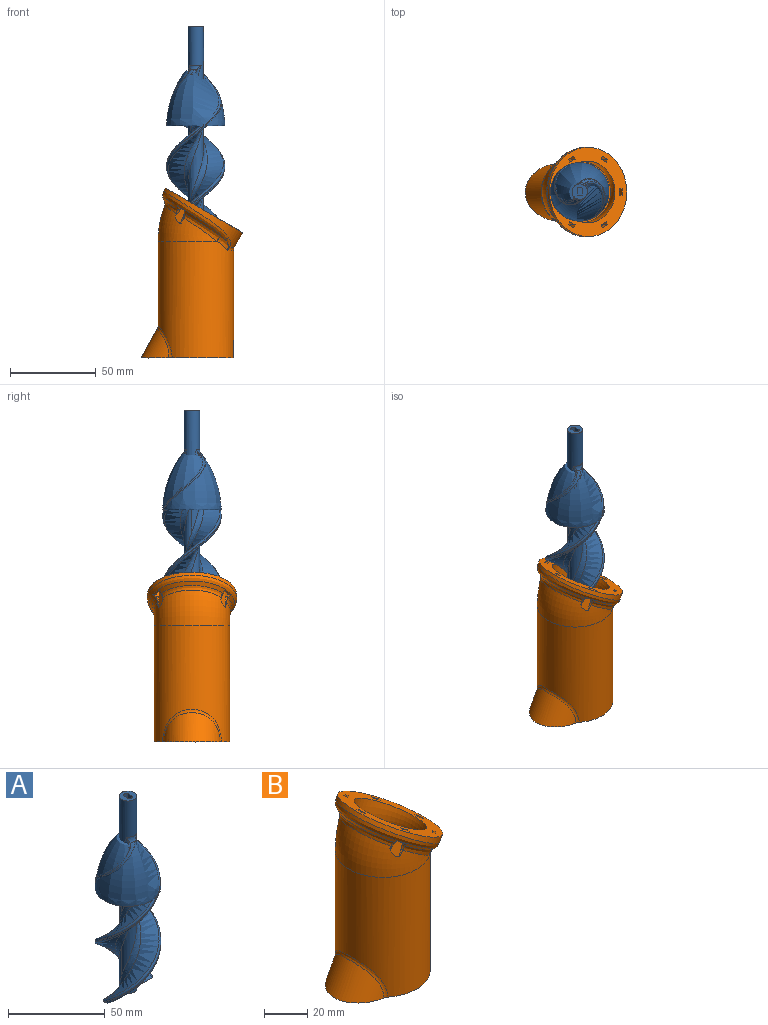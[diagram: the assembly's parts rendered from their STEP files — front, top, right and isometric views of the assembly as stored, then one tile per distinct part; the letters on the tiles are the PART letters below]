
ASSEMBLY  parts=2 mates=1
PART A: 42 faces, bbox 35.1x35.4x126.7 mm
  f0: bspline ~97.14x34.68mm, area 986.1mm2, adj f3,f23,f32,f33
  f1: bspline ~97.14x34.68mm, area 986.1mm2, adj f3,f18,f36,f37
  f2: revolved ~33.25x32.4mm, area 47.3mm2, adj f5,f19,f29,f30,f37,f38
  f3: plane 34.42x9.42mm, normal (0,0,-1), area 165.5mm2, adj f0,f1,f4,f5,f6,f7,f9,f11
  f4: bspline ~97.14x34.68mm, area 1003.5mm2, adj f3,f20,f28,f29
  f5: bspline ~68.57x34.96mm, area 53.1mm2, adj f2,f3,f28,f36
  f6: bspline ~97.14x34.68mm, area 1003.4mm2, adj f3,f21,f24,f25
  f7: bspline ~68.57x34.96mm, area 53.1mm2, adj f3,f8,f24,f32
  f8: revolved ~33.25x32.4mm, area 47.3mm2, adj f7,f22,f25,f26,f33,f34
  f9: cylinder r=4.5mm len=29.09mm, axis (0,0,-1), area 128.4mm2, adj f3,f10,f20,f23
  f10: cylinder r=4.5mm len=111.09mm, axis (0,0,-1), area 1408.2mm2, adj f9,f11,f12,f18,f19,f20,f21,f22
  f11: cylinder r=4.5mm len=69.09mm, axis (0,0,-1), area 385.1mm2, adj f3,f10,f18,f21
  f12: plane 9x9mm, normal (0,0,1), area 49.6mm2, adj f10,f13,f14,f15,f16
  f13: plane 6x4mm, normal (-1,0,0), area 24mm2, adj f12,f14,f16,f17
  f14: cylinder r=2.5mm len=6mm, axis (0,0,1), area 19.3mm2, adj f12,f13,f15,f17
  f15: plane 6x4mm, normal (1,0,0), area 24mm2, adj f12,f14,f16,f17
  f16: cylinder r=2.5mm len=6mm, axis (0,0,1), area 19.3mm2, adj f12,f13,f15,f17
  f17: plane 5x3mm, normal (0,0,1), area 14mm2, adj f13,f14,f15,f16
  f18: bspline ~105.06x13.45mm, area 381.9mm2, adj f1,f3,f10,f11,f38,f39
  f19: torus R=8.5mm, axis (0,0,-1), area 15.5mm2, adj f2,f10,f31,f39
  f20: bspline ~104.2x13.45mm, area 384.1mm2, adj f3,f4,f9,f10,f30,f31
  f21: bspline ~102.31x13.45mm, area 384.3mm2, adj f3,f6,f10,f11,f26,f27
  f22: torus R=8.5mm, axis (0,0,-1), area 15.5mm2, adj f8,f10,f27,f35
  f23: bspline ~105.06x13.45mm, area 381.9mm2, adj f0,f3,f9,f10,f34,f35
  f24: bspline ~68.57x34.03mm, area 161.2mm2, adj f3,f6,f7,f25
  f25: bspline ~30.99x22.88mm, area 57.7mm2, adj f6,f8,f24,f26
  f26: bspline ~4x2.74mm, area 2.8mm2, adj f8,f21,f25,f27
  f27: bspline ~3.03x1.85mm, area 1.1mm2, adj f21,f22,f26
  f28: bspline ~67.17x34.03mm, area 161.2mm2, adj f3,f4,f5,f29
  f29: bspline ~30.99x22.88mm, area 57.7mm2, adj f2,f4,f28,f30
  f30: bspline ~4x2.74mm, area 2.8mm2, adj f2,f20,f29,f31
  f31: bspline ~3.03x1.85mm, area 1.1mm2, adj f19,f20,f30
  f32: bspline ~66.66x34.03mm, area 158.9mm2, adj f0,f3,f7,f33
  f33: bspline ~32.27x24.55mm, area 78.5mm2, adj f0,f8,f32,f34
  f34: bspline ~4.73x4.39mm, area 5.3mm2, adj f8,f23,f33,f35
  f35: bspline ~4.1x4.08mm, area 2.2mm2, adj f22,f23,f34
  f36: bspline ~66.66x34.03mm, area 158.9mm2, adj f1,f3,f5,f37
  f37: bspline ~32.27x24.55mm, area 78.5mm2, adj f1,f2,f36,f38
  f38: bspline ~4.73x4.39mm, area 5.3mm2, adj f2,f18,f37,f39
  f39: bspline ~4.1x4.08mm, area 2.2mm2, adj f18,f19,f38
  f40: cone r=0mm half-angle=59deg, axis (0,0,-1), area 0.9mm2, adj f41
  f41: cylinder r=0.5mm len=16mm, axis (0,0,-1), area 50.3mm2, adj f3,f40
PART B: 99 faces, bbox 82.5x76.7x128.4 mm
  f0: bspline ~32.86x23.26mm, area 40mm2, adj f1,f96,f97,f98
  f1: bspline ~10.45x10.37mm, area 31.2mm2, adj f0,f2,f94,f95,f98
  f2: bspline ~7.8x7.28mm, area 15mm2, adj f1,f3,f94,f96
  f3: cylinder r=26mm len=52mm, axis (-0.5,0,-0.87), area 760.3mm2, adj f2,f4,f39,f93,f96
  f4: bspline ~7.83x7.32mm, area 15mm2, adj f3,f5,f38,f96
  f5: bspline ~10.98x10.44mm, area 31.2mm2, adj f4,f6,f37,f38,f95
  f6: bspline ~32.89x23.2mm, area 40mm2, adj f5,f7,f37,f96
  f7: bspline ~10.89x9.34mm, area 3.4mm2, adj f6,f8,f33,f35,f36
  f8: plane 7.23x3.91mm, normal (-0.75,0.5,0.43), area 13.1mm2, adj f7,f9,f32,f33,f36,f39
  f9: plane 14.25x10.04mm, normal (-0.43,-0.87,0.25), area 56.5mm2, adj f8,f10,f11,f29,f30,f31,f36,f39
  f10: bspline ~11.33x6.26mm, area 1.5mm2, adj f9,f11,f36
  f11: torus R=36mm, axis (0,-1,0), area 1207.8mm2, adj f9,f10,f12,f26,f27,f28,f29,f37
  f12: bspline ~8.15x4.78mm, area 1.5mm2, adj f11,f13,f26
  f13: bspline ~5.26x3.19mm, area 4.6mm2, adj f12,f14,f26,f97,f98
  f14: plane 7.23x3.91mm, normal (-0.75,-0.5,0.43), area 13.1mm2, adj f13,f15,f23,f26,f39,f97
  f15: plane 5.8x5.3mm, normal (0.43,-0.87,-0.25), area 18.8mm2, adj f14,f16,f23,f39
  f16: plane 6.93x3.73mm, normal (0.75,0.5,-0.43), area 12.6mm2, adj f15,f17,f22,f23,f26,f39
  f17: bspline ~10.72x9.26mm, area 3.7mm2, adj f16,f18,f19,f22,f23
  f18: bspline ~1.7x1.56mm, area 0mm2, adj f17,f23,f96
  f19: bspline ~47.13x12.68mm, area 113.1mm2, adj f17,f20,f28,f96
  f20: bspline ~7.67x6.69mm, area 3.7mm2, adj f19,f21,f30,f31,f33
  f21: bspline ~1.68x1.54mm, area 0mm2, adj f20,f33,f96
  f22: bspline ~4.28x2.64mm, area 4.3mm2, adj f16,f17,f26,f27,f28
  f23: bspline ~8.95x6.79mm, area 10.4mm2, adj f14,f15,f16,f17,f18,f24,f25,f96
  f24: bspline ~1.93x1.89mm, area 0mm2, adj f23,f96,f97
  f25: bspline ~10.68x10.59mm, area 0mm2, adj f23,f96
  f26: plane 14.25x10.04mm, normal (-0.43,0.87,0.25), area 56.5mm2, adj f11,f12,f13,f14,f16,f22,f27,f39
  f27: bspline ~9.83x5.76mm, area 0.5mm2, adj f11,f22,f26
  f28: bspline ~36.77x8.08mm, area 110.2mm2, adj f11,f19,f22,f30
  f29: bspline ~9.83x5.76mm, area 0.5mm2, adj f9,f11,f30
  f30: bspline ~4.28x2.64mm, area 4.3mm2, adj f9,f20,f28,f29,f31
  f31: plane 6.93x3.73mm, normal (0.75,-0.5,-0.43), area 12.6mm2, adj f9,f20,f30,f32,f33,f39
  f32: plane 5.8x5.3mm, normal (0.43,0.87,-0.25), area 18.8mm2, adj f8,f31,f33,f39
  f33: bspline ~9.45x7.09mm, area 10.4mm2, adj f7,f8,f20,f21,f31,f32,f34,f35
  f34: bspline ~10.78x10.53mm, area 0mm2, adj f33,f96
  f35: bspline ~1.94x1.9mm, area 0mm2, adj f7,f33,f96
  f36: bspline ~5.13x3.19mm, area 4.6mm2, adj f7,f8,f9,f10,f37
  f37: bspline ~25.15x18.57mm, area 81mm2, adj f5,f6,f11,f36
  f38: bspline ~2.37x1.13mm, area 0.9mm2, adj f4,f5,f93
  f39: plane 52x45.03mm, normal (0.5,0,0.87), area 1057.8mm2, adj f3,f8,f9,f14,f15,f16,f26,f31
  f40: torus R=36mm, axis (0,-1,0), area 2131.8mm2, adj f39,f41
  f41: cylinder r=18mm len=64.33mm, axis (0,0,1), area 6879.1mm2, adj f40,f42,f68,f69,f70,f71,f72
  f42: torus R=5.96mm, axis (0,0,-1), area 4.9mm2, adj f41,f43,f65,f66,f67,f68,f72
  f43: extruded ~28.06x22.68mm, area 553.6mm2, adj f42,f44,f61,f65,f68,f69,f70,f71
  f44: cylinder r=4mm len=2.34mm, axis (-0.48,0,-0.88), area 1.8mm2, adj f43,f45,f59,f60,f61,f71
  f45: sphere r=4mm, area 0.7mm2, adj f44,f46,f58,f71
  f46: bspline ~3.89x1.97mm, area 0mm2, adj f45,f47,f57
  f47: sphere r=18mm, area 51.5mm2, adj f46,f48,f52,f53,f54,f55,f58,f61
  f48: bspline ~3.12x2.56mm, area 1.9mm2, adj f47,f49,f52,f61
  f49: cylinder r=4mm len=0.49mm, axis (0,0,1), area 0.1mm2, adj f48,f50,f51,f61
  f50: plane 0.49x0.27mm, normal (0,1,0), area 0.1mm2, adj f49,f61,f65
  f51: bspline ~2.94x2.51mm, area 0.1mm2, adj f49,f52,f65
  f52: bspline ~3.35x3.16mm, area 3.5mm2, adj f47,f48,f51,f66
  f53: bspline ~3.89x1.97mm, area 0mm2, adj f47,f66,f67
  f54: torus R=19.9mm, axis (0,0,-1), area 98.8mm2, adj f47,f57,f67,f72
  f55: bspline ~3.12x2.56mm, area 1.9mm2, adj f47,f56,f58,f61
  f56: cylinder r=4mm len=0.49mm, axis (0,0,1), area 0.1mm2, adj f55,f59,f60,f61
  f57: bspline ~3.46x3.37mm, area 3.5mm2, adj f46,f54,f71,f72
  f58: bspline ~3.2x3.16mm, area 3.5mm2, adj f45,f47,f55,f60
  f59: plane 0.49x0.27mm, normal (0,-1,0), area 0.1mm2, adj f44,f56,f61
  f60: bspline ~2.94x2.51mm, area 0.1mm2, adj f44,f56,f58
  f61: plane 77.13x67.34mm, normal (0,0,-1), area 1281.1mm2, adj f43,f44,f47,f48,f49,f50,f55,f56
  f62: cylinder r=0.75mm len=4mm, axis (0,0,1), area 18.8mm2, adj f61,f72
  f63: bspline ~34.5x20.08mm, area 105.4mm2, adj f61,f64,f95
  f64: extruded ~32.71x12.38mm, area 0mm2, adj f61,f63
  f65: cylinder r=4mm len=2.34mm, axis (-0.48,0,-0.88), area 1.8mm2, adj f42,f43,f50,f51,f61,f66
  f66: sphere r=4mm, area 0.7mm2, adj f42,f52,f53,f65
  f67: bspline ~3.47x3.37mm, area 3.5mm2, adj f42,f53,f54,f72
  f68: bspline ~3.36x2.02mm, area 1.3mm2, adj f41,f42,f43,f69
  f69: bspline ~29.02x15.34mm, area 79.3mm2, adj f41,f43,f68,f70
  f70: bspline ~3.36x2.02mm, area 1.3mm2, adj f41,f43,f69,f71
  f71: torus R=5.96mm, axis (0,0,-1), area 4.9mm2, adj f41,f43,f44,f45,f57,f70,f72
  f72: plane 36x27.54mm, normal (0,0,1), area 673.3mm2, adj f41,f42,f54,f57,f62,f67,f71
  f73: plane 4.83x3.37mm, normal (0.75,0.5,-0.43), area 10mm2, adj f39,f74,f75,f77
  f74: plane 3.87x3.73mm, normal (0.5,0,0.87), area 8mm2, adj f73,f75,f76,f77
  f75: plane 6.06x5.5mm, normal (-0.43,0.87,0.25), area 20mm2, adj f39,f73,f74,f76
  f76: plane 4.83x3.37mm, normal (-0.75,-0.5,0.43), area 10mm2, adj f39,f74,f75,f77
  f77: plane 6.06x5.5mm, normal (0.43,-0.87,-0.25), area 20mm2, adj f39,f73,f74,f76
  f78: plane 4.83x3.37mm, normal (-0.75,0.5,0.43), area 10mm2, adj f39,f79,f80,f82
  f79: plane 3.87x3.73mm, normal (0.5,0,0.87), area 8mm2, adj f78,f80,f81,f82
  f80: plane 6.06x5.5mm, normal (-0.43,-0.87,0.25), area 20mm2, adj f39,f78,f79,f81
  f81: plane 4.83x3.37mm, normal (0.75,-0.5,-0.43), area 10mm2, adj f39,f79,f80,f82
  f82: plane 6.06x5.5mm, normal (0.43,0.87,-0.25), area 20mm2, adj f39,f78,f79,f81
  f83: plane 5.33x4.23mm, normal (0,1,0), area 10mm2, adj f39,f84,f85,f87
  f84: plane 4x1.73mm, normal (0.5,0,0.87), area 8mm2, adj f83,f85,f86,f87
  f85: plane 4.33x4mm, normal (-0.87,0,0.5), area 20mm2, adj f39,f83,f84,f86
  f86: plane 5.33x4.23mm, normal (0,-1,0), area 10mm2, adj f39,f84,f85,f87
  f87: plane 4.33x4mm, normal (0.87,0,-0.5), area 20mm2, adj f39,f83,f84,f86
  f88: plane 4.33x4mm, normal (-0.87,0,0.5), area 20mm2, adj f39,f89,f90,f92
  f89: plane 4x1.73mm, normal (0.5,0,0.87), area 8mm2, adj f88,f90,f91,f92
  f90: plane 5.33x4.23mm, normal (0,-1,0), area 10mm2, adj f39,f88,f89,f91
  f91: plane 4.33x4mm, normal (0.87,0,-0.5), area 20mm2, adj f39,f89,f90,f92
  f92: plane 5.33x4.23mm, normal (0,1,0), area 10mm2, adj f39,f88,f89,f91
  f93: bspline ~27.31x5.11mm, area 48.2mm2, adj f3,f38,f94,f95
  f94: bspline ~3x1.54mm, area 0.9mm2, adj f1,f2,f93
  f95: cylinder r=22mm len=68mm, axis (0,0,1), area 8639.8mm2, adj f1,f5,f11,f61,f63,f93
  f96: bspline ~52.02x40.05mm, area 399.7mm2, adj f0,f2,f3,f4,f6,f18,f19,f21
  f97: bspline ~10.89x9.34mm, area 3.4mm2, adj f0,f13,f14,f23,f24
  f98: bspline ~24.02x17.84mm, area 81mm2, adj f0,f1,f11,f13
PLACE A rot(axis=(0,0,-1),0.7deg) t=(31.78,-0.03,71.42)mm
PLACE B t=(31.78,-0.03,0)mm
MATE cylindrical A.f9 <-> B.f95  axis (0,0,-1) through (31.78,-0.03,71.42)mm
